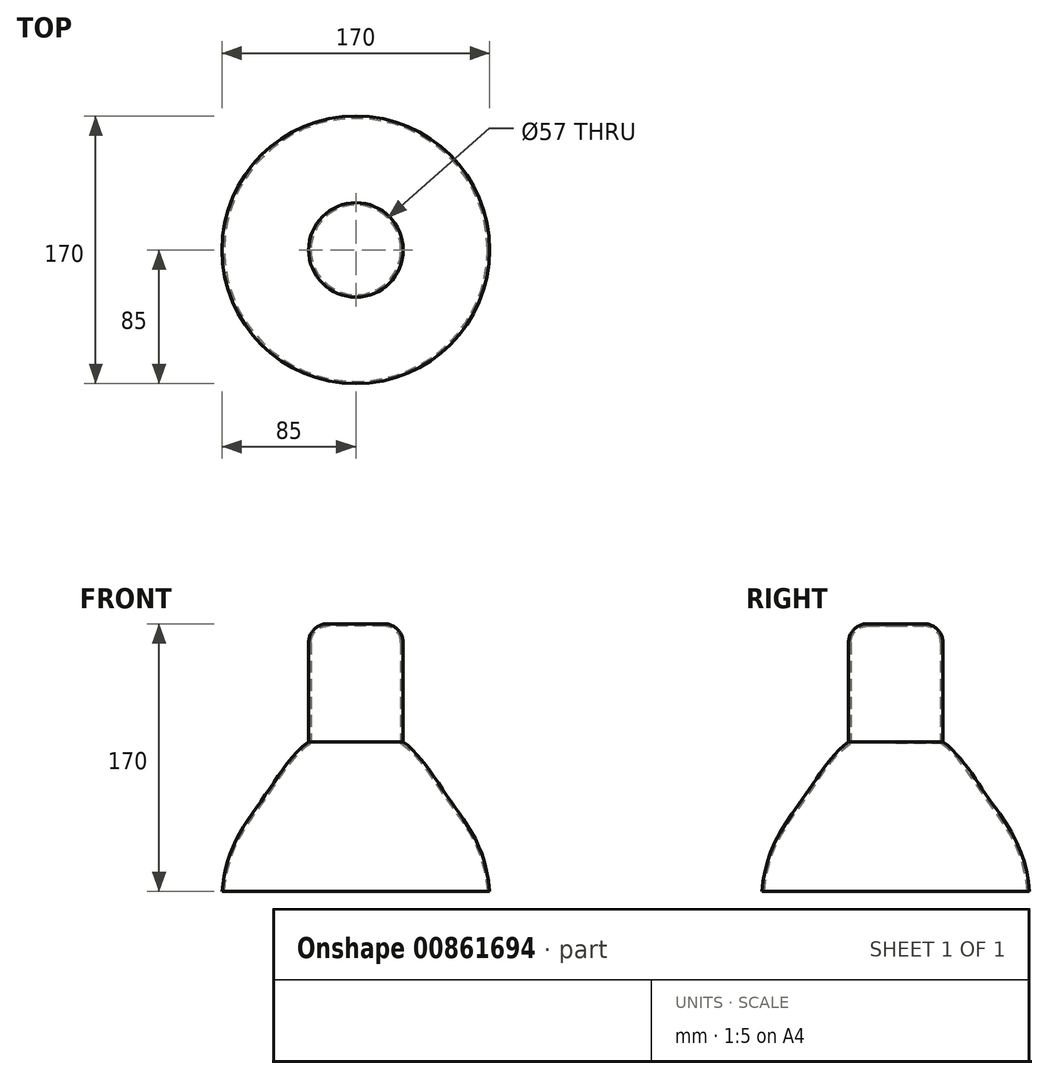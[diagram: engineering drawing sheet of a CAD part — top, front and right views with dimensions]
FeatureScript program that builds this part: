
annotation { "Feature Type Name" : "Feature", "Feature Type Description" : "" }
export const myFeature = defineFeature(function(context is Context, id is Id, definition is map)
    precondition{}
    {
        {
            var Q0;
            Q0=qCreatedBy(makeId("Top.planeOp"),FACE);
            var sketch = newSketch(context, id + "F0", { "sketchPlane" : qUnion([Q0])});
            skCircle(sketch, "E0", {"center": v(0, 0) * mm, "radius": 85 * mm});
            skSolve(sketch);
        }
        {
            var Q0;
            Q0=makeQuery(id+"F0.imprint","IMPRINT",FACE,{"disambiguationData":[TD([[makeQuery(id+"F0.imprint","IMPRINT",EDGE,{"derivedFrom":sQuery(id+"F0.wireOp",EDGE,"E0")}),1.0]])]});
            cPlane(context, id + "F1", {"entities" : qUnion([Q0]), "cplaneType" : CPlaneType.OFFSET, "offset" : 95 * mm, "width" : 150 * mm, "height" : 150 * mm});
        }
        {
            var Q0;
            Q0=qCreatedBy(id+"F1.planeOp",FACE);
            var sketch = newSketch(context, id + "F2", { "sketchPlane" : qUnion([Q0])});
            skCircle(sketch, "E1", {"center": v(0, 0) * mm, "radius": 30 * mm});
            skSolve(sketch);
        }
        {
            var Q0;
            Q0=qCreatedBy(makeId("Right.planeOp"),FACE);
            var sketch = newSketch(context, id + "F3", { "sketchPlane" : qUnion([Q0])});
            skLineSegment(sketch, "E2.0", {"start": v(-30, 95) * mm, "end": v(30, 95) * mm});
            skLineSegment(sketch, "E3.0", {"start": v(-85, 0) * mm, "end": v(85, 0) * mm});
            skFitSpline(sketch, "E4", {"points": [v(-30, 95) * mm, v(-59.22, 58.76) * mm, v(-85, 0) * mm], "startDerivative": vector(-72.6, -50.95) * mm, "endDerivative": vector(-13.55, -159.44) * mm});
            skLineSegment(sketch, "E5", {"start": v(0, 95) * mm, "end": v(0, 0) * mm});
            skSolve(sketch);
        }
        {
            var Q0;
            {var subQ0=sQuery(id+"F3.wireOp",EDGE,"E4");Q0=makeQuery(id+"F3.imprint","IMPRINT",FACE,{"disambiguationData":[TD([[makeQuery(id+"F3.imprint","IMPRINT",EDGE,{"derivedFrom":subQ0}),1.0]])]});}
            var Q1;
            Q1=sQuery(id+"F3.wireOp",EDGE,"E5");
            revolve(context, id + "F4", {"surfaceOperationType" : NewSurfaceOperationType.NEW, "entities" : qUnion([Q0]), "axis" : qUnion([Q1]), "revolveType" : RevolveType.FULL});
        }
        {
            var Q0;
            Q0=makeQuery(id+"F2.imprint","IMPRINT",FACE,{"disambiguationData":[TD([[makeQuery(id+"F2.imprint","IMPRINT",EDGE,{"derivedFrom":sQuery(id+"F2.wireOp",EDGE,"E1")}),1.0]])]});
            extrude(context, id + "F5", {"entities" : qUnion([Q0]), "operationType" : NewBodyOperationType.ADD, "depth" : 75 * mm, "offsetDistance" : 25 * mm});
        }
        {
            var Q0;
            Q0=makeQuery(id+"F5.opExtrude","CAP_EDGE",EDGE,{"disambiguationData":[OSD([sQuery(id+"F2.wireOp",EDGE,"E1")])],"isStart":false});
            fillet(context, id + "F6", {"entities" : qUnion([Q0]), "radius" : 12 * mm, "tangentPropagation" : true, "allowEdgeOverflow" : false});
        }
        {
            var Q0;
            Q0=makeQuery(id+"F4.opRevolve","SWEPT_FACE",FACE,{"disambiguationData":[OSD([sQuery(id+"F3.wireOp",EDGE,"E3.0")])]});
            shell(context, id + "F7", {"entities" : qUnion([Q0]), "thickness" : 1.5 * mm});
        }
    });
